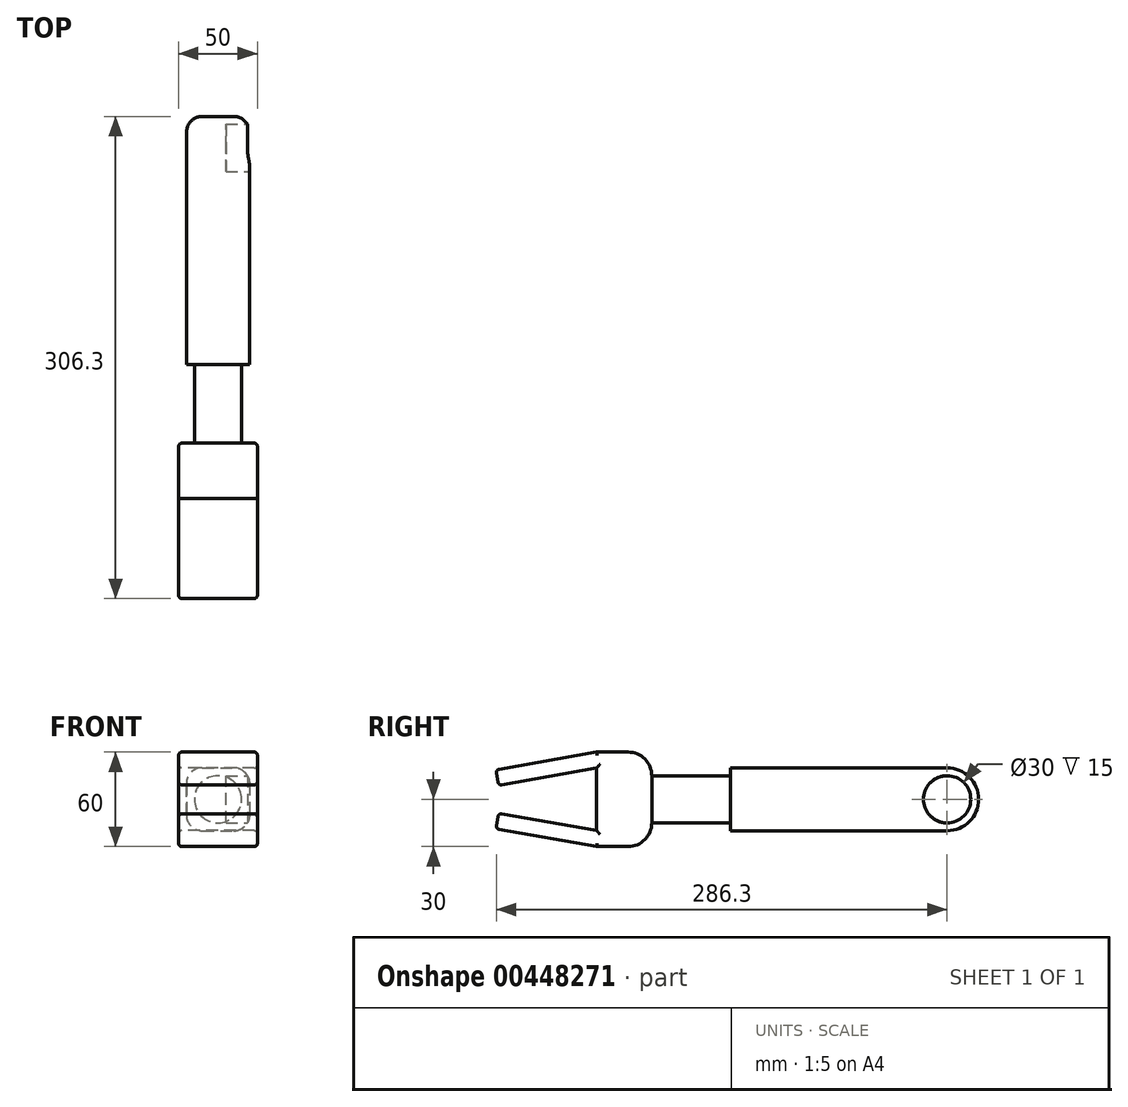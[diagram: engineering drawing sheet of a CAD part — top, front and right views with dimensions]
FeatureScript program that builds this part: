
annotation { "Feature Type Name" : "Feature", "Feature Type Description" : "" }
export const myFeature = defineFeature(function(context is Context, id is Id, definition is map)
    precondition{}
    {
        {
            var Q0;
            Q0=qCreatedBy(makeId("Front.planeOp"),FACE);
            var sketch = newSketch(context, id + "F0", { "sketchPlane" : qUnion([Q0])});
            skLineSegment(sketch, "E0.bottom", {"start": v(-20, 20) * mm, "end": v(20, 20) * mm});
            skLineSegment(sketch, "E0.top", {"start": v(-20, -20) * mm, "end": v(20, -20) * mm});
            skLineSegment(sketch, "E0.left", {"start": v(-20, 20) * mm, "end": v(-20, -20) * mm});
            skLineSegment(sketch, "E0.right", {"start": v(20, 20) * mm, "end": v(20, -20) * mm});
            skSolve(sketch);
        }
        {
            var Q0;
            Q0=makeQuery(id+"F0.imprint","IMPRINT",FACE,{"disambiguationData":[TD([[makeQuery(id+"F0.imprint","IMPRINT",EDGE,{"derivedFrom":sQuery(id+"F0.wireOp",EDGE,"E0.bottom")}),-1.0]])]});
            extrude(context, id + "F1", {"entities" : qUnion([Q0]), "depth" : 157.6 * mm});
        }
        {
            var Q0;
            Q0=makeQuery(id+"F1.opExtrude","SWEPT_FACE",FACE,{"disambiguationData":[OSD([sQuery(id+"F0.wireOp",EDGE,"E0.right")])]});
            var sketch = newSketch(context, id + "F2", { "sketchPlane" : qUnion([Q0])});
            skCircle(sketch, "E1", {"center": v(-20, 0) * mm, "radius": 15 * mm});
            skSolve(sketch);
        }
        {
            var Q0;
            Q0=makeQuery(id+"F2.imprint","IMPRINT",FACE,{"disambiguationData":[TD([[makeQuery(id+"F2.imprint","IMPRINT",EDGE,{"derivedFrom":sQuery(id+"F2.wireOp",EDGE,"E1")}),1.0]])]});
            extrude(context, id + "F3", {"entities" : qUnion([Q0]), "operationType" : NewBodyOperationType.REMOVE, "oppositeDirection" : true, "depth" : 15 * mm});
        }
        {
            var Q0;
            Q0=makeQuery(id+"F1.opExtrude","CAP_EDGE",EDGE,{"disambiguationData":[OSD([sQuery(id+"F0.wireOp",EDGE,"E0.bottom")])],"isStart":true});
            var Q1;
            Q1=makeQuery(id+"F1.opExtrude","CAP_EDGE",EDGE,{"disambiguationData":[OSD([sQuery(id+"F0.wireOp",EDGE,"E0.top")])],"isStart":true});
            fillet(context, id + "F4", {"entities" : qUnion([Q0, Q1]), "radius" : 20 * mm, "tangentPropagation" : true, "allowEdgeOverflow" : false});
        }
        {
            var Q0;
            Q0=makeQuery(id+"F1.opExtrude","SWEPT_EDGE",EDGE,{"disambiguationData":[OSD([sQuery(id+"F0.wireOp",EDGE,"E0.bottom"),sQuery(id+"F0.wireOp",EDGE,"E0.left")])]});
            var Q1;
            Q1=makeQuery(id+"F1.opExtrude","SWEPT_EDGE",EDGE,{"disambiguationData":[OSD([sQuery(id+"F0.wireOp",EDGE,"E0.bottom"),sQuery(id+"F0.wireOp",EDGE,"E0.right")])]});
            fillet(context, id + "F5", {"entities" : qUnion([Q0, Q1]), "radius" : 10 * mm, "tangentPropagation" : true, "allowEdgeOverflow" : false});
        }
        {
            var Q0;
            Q0=makeQuery(id+"F1.opExtrude","CAP_FACE",FACE,{"disambiguationData":[OSD([sQuery(id+"F0.wireOp",EDGE,"E0.bottom"),sQuery(id+"F0.wireOp",EDGE,"E0.top"),sQuery(id+"F0.wireOp",EDGE,"E0.left"),sQuery(id+"F0.wireOp",EDGE,"E0.right")])],"isStart":false});
            var sketch = newSketch(context, id + "F6", { "sketchPlane" : qUnion([Q0])});
            skCircle(sketch, "E2", {"center": v(0, 0) * mm, "radius": 15 * mm});
            skSolve(sketch);
        }
        {
            var Q0;
            Q0=makeQuery(id+"F6.imprint","IMPRINT",FACE,{"disambiguationData":[TD([[makeQuery(id+"F6.imprint","IMPRINT",EDGE,{"derivedFrom":sQuery(id+"F6.wireOp",EDGE,"E2")}),1.0]])]});
            extrude(context, id + "F7", {"entities" : qUnion([Q0]), "operationType" : NewBodyOperationType.ADD, "depth" : 50 * mm});
        }
        {
            var Q0;
            Q0=qCreatedBy(makeId("Right.planeOp"),FACE);
            var sketch = newSketch(context, id + "F8", { "sketchPlane" : qUnion([Q0])});
            skLineSegment(sketch, "E3", {"start": v(-207.6, 0) * mm, "end": v(-207.6, 30) * mm});
            skLineSegment(sketch, "E4", {"start": v(-207.6, 30) * mm, "end": v(-242.6, 30) * mm});
            skLineSegment(sketch, "E5", {"start": v(-242.6, 30) * mm, "end": v(-242.6, -30) * mm});
            skLineSegment(sketch, "E6", {"start": v(-242.6, -30) * mm, "end": v(-207.6, -30) * mm});
            skLineSegment(sketch, "E7", {"start": v(-207.6, -30) * mm, "end": v(-207.6, 0) * mm});
            skLineSegment(sketch, "E8", {"start": v(-242.6, 30) * mm, "end": v(-306.61, 18.71) * mm});
            skLineSegment(sketch, "E9", {"start": v(-306.61, 18.71) * mm, "end": v(-304.88, 8.86) * mm});
            skLineSegment(sketch, "E10", {"start": v(-304.88, 8.86) * mm, "end": v(-242.6, 19.85) * mm});
            skLineSegment(sketch, "E11", {"start": v(-242.6, 30) * mm, "end": v(-352.31, 30) * mm, "construction": true});
            skLineSegment(sketch, "E12", {"start": v(-242.6, -30) * mm, "end": v(-306.61, -18.71) * mm});
            skLineSegment(sketch, "E13", {"start": v(-306.61, -18.71) * mm, "end": v(-304.88, -8.86) * mm});
            skLineSegment(sketch, "E14", {"start": v(-304.88, -8.86) * mm, "end": v(-242.6, -19.85) * mm});
            skLineSegment(sketch, "E15", {"start": v(-242.6, -30) * mm, "end": v(-402.29, -30) * mm, "construction": true});
            skSolve(sketch);
        }
        {
            var Q0;
            Q0=makeQuery(id+"F8.imprint","IMPRINT",FACE,{"disambiguationData":[TD([[makeQuery(id+"F8.imprint","IMPRINT",EDGE,{"derivedFrom":sQuery(id+"F8.wireOp",EDGE,"E3")}),1.0]])]});
            var Q1;
            {var subQ0=sQuery(id+"F8.wireOp",EDGE,"E8");Q1=makeQuery(id+"F8.imprint","IMPRINT",FACE,{"disambiguationData":[TD([[makeQuery(id+"F8.imprint","IMPRINT",EDGE,{"derivedFrom":subQ0}),1.0]])]});}
            var Q2;
            {var subQ0=sQuery(id+"F8.wireOp",EDGE,"E12");Q2=makeQuery(id+"F8.imprint","IMPRINT",FACE,{"disambiguationData":[TD([[makeQuery(id+"F8.imprint","IMPRINT",EDGE,{"derivedFrom":subQ0}),-1.0]])]});}
            extrude(context, id + "F9", {"entities" : qUnion([Q0, Q1, Q2]), "operationType" : NewBodyOperationType.ADD, "depth" : 25 * mm});
        }
        {
            var Q0;
            Q0=makeQuery(id+"F9.opExtrude","CAP_FACE",FACE,{"disambiguationData":[OSD([sQuery(id+"F8.wireOp",EDGE,"E3"),sQuery(id+"F8.wireOp",EDGE,"E4"),sQuery(id+"F8.wireOp",EDGE,"E5"),sQuery(id+"F8.wireOp",EDGE,"E6"),sQuery(id+"F8.wireOp",EDGE,"E7"),sQuery(id+"F8.wireOp",EDGE,"E8"),sQuery(id+"F8.wireOp",EDGE,"E9"),sQuery(id+"F8.wireOp",EDGE,"E10"),sQuery(id+"F8.wireOp",EDGE,"E12"),sQuery(id+"F8.wireOp",EDGE,"E13"),sQuery(id+"F8.wireOp",EDGE,"E14")])],"isStart":true});
            extrude(context, id + "F10", {"entities" : qUnion([Q0]), "operationType" : NewBodyOperationType.ADD, "depth" : 25 * mm});
        }
        {
            var Q0;
            {var subQ0=sQuery(id+"F8.wireOp",EDGE,"E4");var subQ1=sQuery(id+"F8.wireOp",EDGE,"E3");Q0=makeQuery(id+"F10.boolean.opBoolean","MERGE",EDGE,{"derivedFrom":[makeQuery(id+"F9.opExtrude","SWEPT_EDGE",EDGE,{"disambiguationData":[OSD([subQ1,subQ0])]}),makeQuery(id+"F10.opExtrude","SWEPT_EDGE",EDGE,{"disambiguationData":[OSD([subQ1,subQ0])]})]});}
            var Q1;
            {var subQ0=sQuery(id+"F8.wireOp",EDGE,"E7");var subQ1=sQuery(id+"F8.wireOp",EDGE,"E6");Q1=makeQuery(id+"F10.boolean.opBoolean","MERGE",EDGE,{"derivedFrom":[makeQuery(id+"F9.opExtrude","SWEPT_EDGE",EDGE,{"disambiguationData":[OSD([subQ1,subQ0])]}),makeQuery(id+"F10.opExtrude","SWEPT_EDGE",EDGE,{"disambiguationData":[OSD([subQ1,subQ0])]})]});}
            fillet(context, id + "F11", {"entities" : qUnion([Q0, Q1]), "radius" : 15 * mm, "tangentPropagation" : true, "allowEdgeOverflow" : false});
        }
        {
            var Q0;
            Q0=makeQuery(id+"F10.opExtrude","CAP_FACE",FACE,{"disambiguationData":[OSD([sQuery(id+"F8.wireOp",EDGE,"E3"),sQuery(id+"F8.wireOp",EDGE,"E4"),sQuery(id+"F8.wireOp",EDGE,"E5"),sQuery(id+"F8.wireOp",EDGE,"E6"),sQuery(id+"F8.wireOp",EDGE,"E7"),sQuery(id+"F8.wireOp",EDGE,"E8"),sQuery(id+"F8.wireOp",EDGE,"E9"),sQuery(id+"F8.wireOp",EDGE,"E10"),sQuery(id+"F8.wireOp",EDGE,"E12"),sQuery(id+"F8.wireOp",EDGE,"E13"),sQuery(id+"F8.wireOp",EDGE,"E14")])],"isStart":false});
            var Q1;
            Q1=makeQuery(id+"F9.opExtrude","CAP_FACE",FACE,{"disambiguationData":[OSD([sQuery(id+"F8.wireOp",EDGE,"E3"),sQuery(id+"F8.wireOp",EDGE,"E4"),sQuery(id+"F8.wireOp",EDGE,"E5"),sQuery(id+"F8.wireOp",EDGE,"E6"),sQuery(id+"F8.wireOp",EDGE,"E7"),sQuery(id+"F8.wireOp",EDGE,"E8"),sQuery(id+"F8.wireOp",EDGE,"E9"),sQuery(id+"F8.wireOp",EDGE,"E10"),sQuery(id+"F8.wireOp",EDGE,"E12"),sQuery(id+"F8.wireOp",EDGE,"E13"),sQuery(id+"F8.wireOp",EDGE,"E14")])],"isStart":false});
            var Q2;
            {var subQ0=sQuery(id+"F8.wireOp",EDGE,"E9");var subQ1=sQuery(id+"F8.wireOp",EDGE,"E8");Q2=makeQuery(id+"F10.boolean.opBoolean","MERGE",EDGE,{"derivedFrom":[makeQuery(id+"F9.opExtrude","SWEPT_EDGE",EDGE,{"disambiguationData":[OSD([subQ1,subQ0])]}),makeQuery(id+"F10.opExtrude","SWEPT_EDGE",EDGE,{"disambiguationData":[OSD([subQ1,subQ0])]})]});}
            var Q3;
            {var subQ0=sQuery(id+"F8.wireOp",EDGE,"E10");var subQ1=sQuery(id+"F8.wireOp",EDGE,"E9");Q3=makeQuery(id+"F10.boolean.opBoolean","MERGE",EDGE,{"derivedFrom":[makeQuery(id+"F9.opExtrude","SWEPT_EDGE",EDGE,{"disambiguationData":[OSD([subQ1,subQ0])]}),makeQuery(id+"F10.opExtrude","SWEPT_EDGE",EDGE,{"disambiguationData":[OSD([subQ1,subQ0])]})]});}
            var Q4;
            {var subQ0=sQuery(id+"F8.wireOp",EDGE,"E14");var subQ1=sQuery(id+"F8.wireOp",EDGE,"E13");Q4=makeQuery(id+"F10.boolean.opBoolean","MERGE",EDGE,{"derivedFrom":[makeQuery(id+"F9.opExtrude","SWEPT_EDGE",EDGE,{"disambiguationData":[OSD([subQ1,subQ0])]}),makeQuery(id+"F10.opExtrude","SWEPT_EDGE",EDGE,{"disambiguationData":[OSD([subQ1,subQ0])]})]});}
            var Q5;
            {var subQ0=sQuery(id+"F8.wireOp",EDGE,"E13");var subQ1=sQuery(id+"F8.wireOp",EDGE,"E12");Q5=makeQuery(id+"F10.boolean.opBoolean","MERGE",EDGE,{"derivedFrom":[makeQuery(id+"F9.opExtrude","SWEPT_EDGE",EDGE,{"disambiguationData":[OSD([subQ1,subQ0])]}),makeQuery(id+"F10.opExtrude","SWEPT_EDGE",EDGE,{"disambiguationData":[OSD([subQ1,subQ0])]})]});}
            fillet(context, id + "F12", {"entities" : qUnion([Q0, Q1, Q2, Q3, Q4, Q5]), "radius" : 2 * mm, "tangentPropagation" : true, "allowEdgeOverflow" : false});
        }
    });
